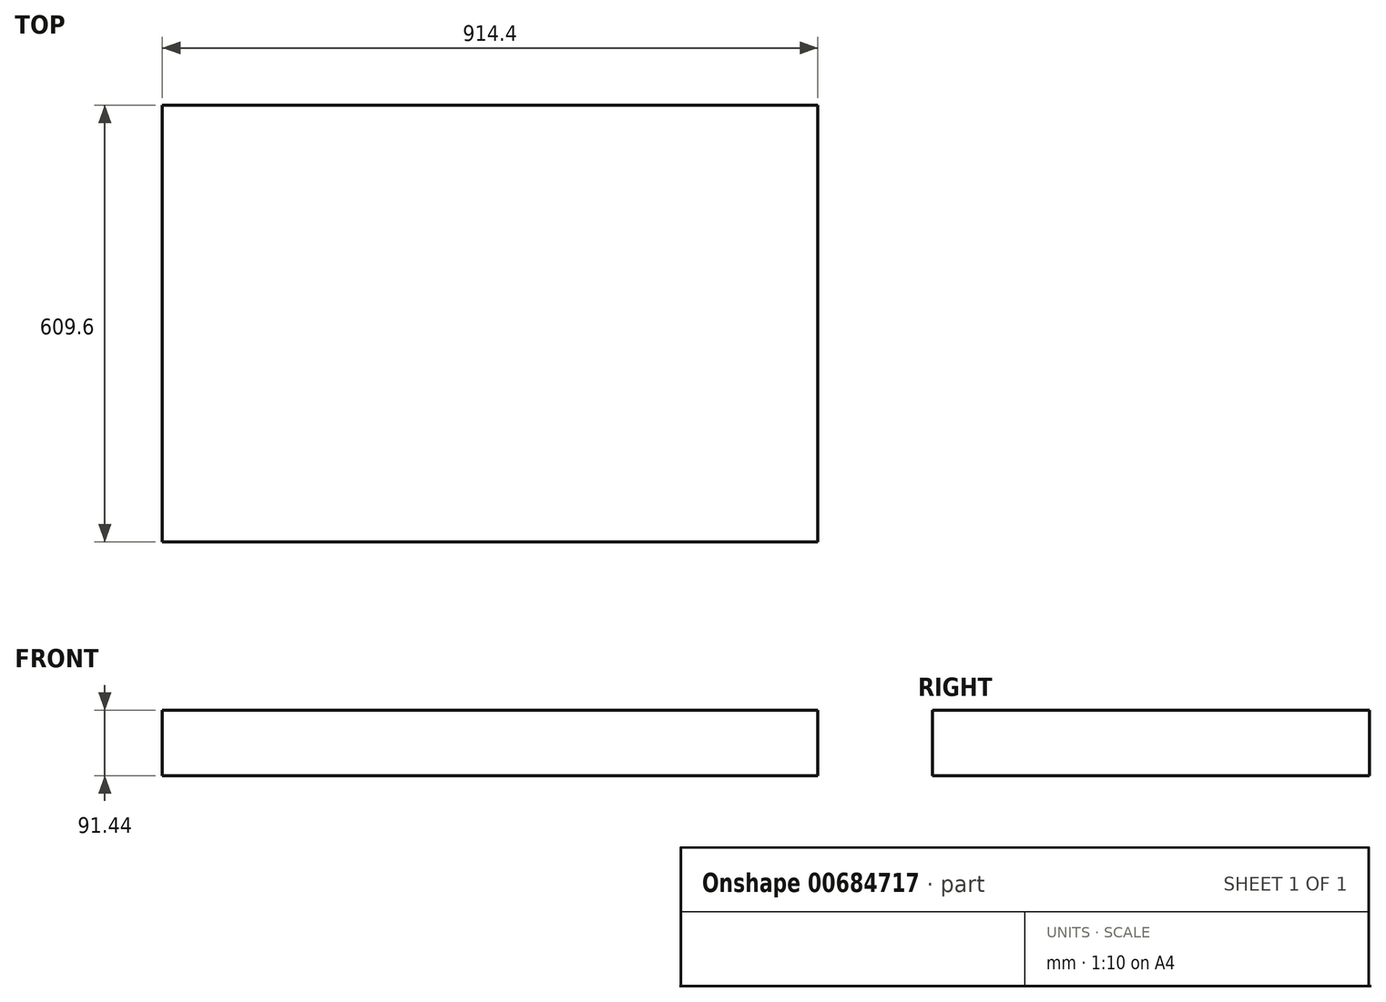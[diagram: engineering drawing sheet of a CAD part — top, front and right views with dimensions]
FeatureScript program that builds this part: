
annotation { "Feature Type Name" : "Feature", "Feature Type Description" : "" }
export const myFeature = defineFeature(function(context is Context, id is Id, definition is map)
    precondition{}
    {
        {
            var Q0;
            Q0=qCreatedBy(makeId("Top.planeOp"),FACE);
            var sketch = newSketch(context, id + "F0", { "sketchPlane" : qUnion([Q0])});
            skLineSegment(sketch, "E0", {"start": v(0, 0) * mm, "end": v(0, -609.6) * mm});
            skLineSegment(sketch, "E1", {"start": v(0, -609.6) * mm, "end": v(914.4, -609.6) * mm});
            skLineSegment(sketch, "E2", {"start": v(914.4, -609.6) * mm, "end": v(914.4, 0) * mm});
            skLineSegment(sketch, "E3", {"start": v(914.4, 0) * mm, "end": v(0, 0) * mm});
            skSolve(sketch);
        }
        {
            var Q0;
            Q0 = qSketchRegion(id + "F0", true);
            extrude(context, id + "F1", {"entities" : qUnion([Q0]), "depth" : 91.44 * mm, "offsetDistance" : 30.48 * mm});
        }
    });
